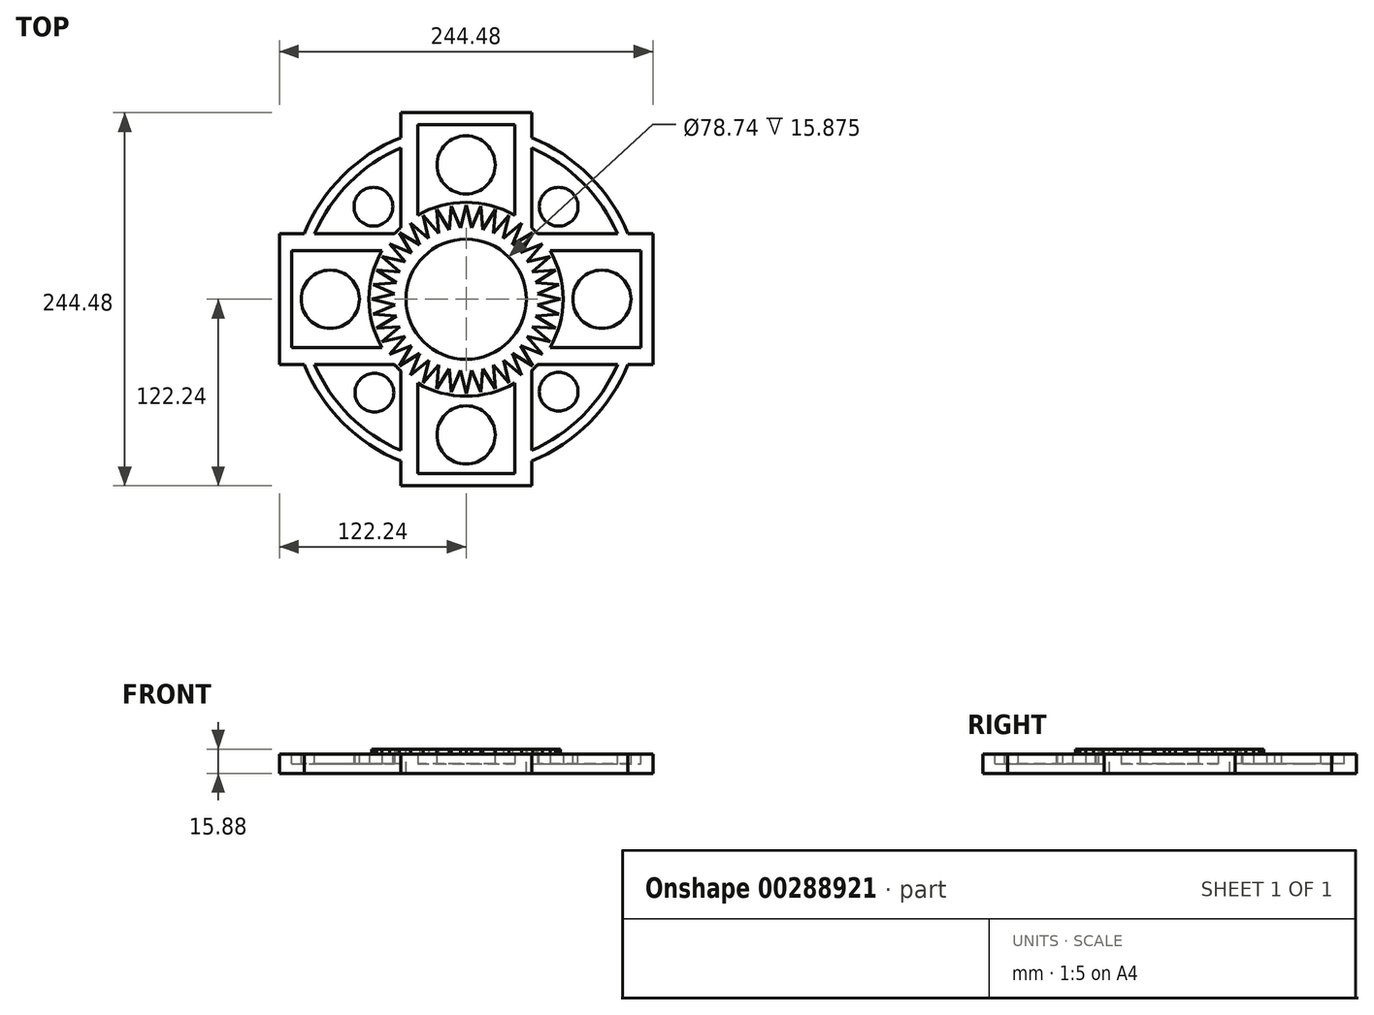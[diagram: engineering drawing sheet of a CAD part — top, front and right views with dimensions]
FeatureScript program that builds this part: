
annotation { "Feature Type Name" : "Feature", "Feature Type Description" : "" }
export const myFeature = defineFeature(function(context is Context, id is Id, definition is map)
    precondition{}
    {
        {
            var Q0;
            Q0=qCreatedBy(makeId("Top.planeOp"),FACE);
            var sketch = newSketch(context, id + "F0", { "sketchPlane" : qUnion([Q0])});
            skArc(sketch, "E0", {"start": v(-42.86, 105.96) * mm, "mid": v(-80.82, -80.82) * mm, "end": v(105.96, -42.86) * mm});
            skLineSegment(sketch, "E1.bottom", {"start": v(122.24, -122.24) * mm, "end": v(-122.24, -122.24) * mm, "construction": true});
            skLineSegment(sketch, "E1.top", {"start": v(122.24, 122.24) * mm, "end": v(-122.24, 122.24) * mm, "construction": true});
            skLineSegment(sketch, "E1.left", {"start": v(122.24, -122.24) * mm, "end": v(122.24, 122.24) * mm, "construction": true});
            skLineSegment(sketch, "E1.right", {"start": v(-122.24, -122.24) * mm, "end": v(-122.24, 122.24) * mm, "construction": true});
            skLineSegment(sketch, "E2.bottom", {"start": v(-42.86, 122.24) * mm, "end": v(42.86, 122.24) * mm});
            skLineSegment(sketch, "E2.top", {"start": v(-42.86, -122.24) * mm, "end": v(42.86, -122.24) * mm});
            skLineSegment(sketch, "E2.left", {"start": v(-42.86, 122.24) * mm, "end": v(-42.86, 105.96) * mm});
            skLineSegment(sketch, "E2.right", {"start": v(42.86, 122.24) * mm, "end": v(42.86, 105.96) * mm});
            skLineSegment(sketch, "E3.bottom", {"start": v(-122.24, 42.86) * mm, "end": v(-105.96, 42.86) * mm});
            skLineSegment(sketch, "E3.top", {"start": v(-122.24, -42.86) * mm, "end": v(-105.96, -42.86) * mm});
            skLineSegment(sketch, "E3.left", {"start": v(-122.24, 42.86) * mm, "end": v(-122.24, -42.86) * mm});
            skLineSegment(sketch, "E3.right", {"start": v(122.24, 42.86) * mm, "end": v(122.24, -42.86) * mm});
            skLineSegment(sketch, "E4.trimOffspring", {"start": v(105.96, 42.86) * mm, "end": v(122.24, 42.86) * mm});
            skArc(sketch, "E5.trimOffspring", {"start": v(105.96, 42.86) * mm, "mid": v(80.82, 80.82) * mm, "end": v(42.86, 105.96) * mm});
            skLineSegment(sketch, "E6.trimOffspring", {"start": v(105.96, -42.86) * mm, "end": v(122.24, -42.86) * mm});
            skLineSegment(sketch, "E7.trimOffspring", {"start": v(42.86, -105.96) * mm, "end": v(42.86, -122.24) * mm});
            skLineSegment(sketch, "E8.trimOffspring", {"start": v(-42.86, -105.96) * mm, "end": v(-42.86, -122.24) * mm});
            skSolve(sketch);
        }
        {
            var Q0;
            Q0 = qSketchRegion(id + "F0", true);
            extrude(context, id + "F1", {"entities" : qUnion([Q0]), "depth" : 12.7 * mm});
        }
        {
            var Q0;
            Q0=makeQuery(id+"F1.opExtrude","CAP_FACE",FACE,{"disambiguationData":[OSD([sQuery(id+"F0.wireOp",EDGE,"E0"),sQuery(id+"F0.wireOp",EDGE,"E2.bottom"),sQuery(id+"F0.wireOp",EDGE,"E2.top"),sQuery(id+"F0.wireOp",EDGE,"E2.left"),sQuery(id+"F0.wireOp",EDGE,"E2.right"),sQuery(id+"F0.wireOp",EDGE,"E3.bottom"),sQuery(id+"F0.wireOp",EDGE,"E3.top"),sQuery(id+"F0.wireOp",EDGE,"E3.left"),sQuery(id+"F0.wireOp",EDGE,"E3.right"),sQuery(id+"F0.wireOp",EDGE,"E4.trimOffspring"),sQuery(id+"F0.wireOp",EDGE,"E5.trimOffspring"),sQuery(id+"F0.wireOp",EDGE,"E6.trimOffspring"),sQuery(id+"F0.wireOp",EDGE,"E7.trimOffspring"),sQuery(id+"F0.wireOp",EDGE,"E8.trimOffspring")])],"isStart":false});
            var sketch = newSketch(context, id + "F2", { "sketchPlane" : qUnion([Q0])});
            skCircle(sketch, "E9", {"center": v(0, 0) * mm, "radius": 39.37 * mm});
            skSolve(sketch);
        }
        {
            var Q0;
            Q0 = qSketchRegion(id + "F2", true);
            extrude(context, id + "F3", {"entities" : qUnion([Q0]), "operationType" : NewBodyOperationType.REMOVE, "endBound" : BoundingType.UP_TO_NEXT, "oppositeDirection" : true, "depth" : 25.4 * mm});
        }
        {
            var Q0;
            Q0=makeQuery(id+"F1.opExtrude","CAP_FACE",FACE,{"disambiguationData":[OSD([sQuery(id+"F0.wireOp",EDGE,"E0"),sQuery(id+"F0.wireOp",EDGE,"E2.bottom"),sQuery(id+"F0.wireOp",EDGE,"E2.top"),sQuery(id+"F0.wireOp",EDGE,"E2.left"),sQuery(id+"F0.wireOp",EDGE,"E2.right"),sQuery(id+"F0.wireOp",EDGE,"E3.bottom"),sQuery(id+"F0.wireOp",EDGE,"E3.top"),sQuery(id+"F0.wireOp",EDGE,"E3.left"),sQuery(id+"F0.wireOp",EDGE,"E3.right"),sQuery(id+"F0.wireOp",EDGE,"E4.trimOffspring"),sQuery(id+"F0.wireOp",EDGE,"E5.trimOffspring"),sQuery(id+"F0.wireOp",EDGE,"E6.trimOffspring"),sQuery(id+"F0.wireOp",EDGE,"E7.trimOffspring"),sQuery(id+"F0.wireOp",EDGE,"E8.trimOffspring")])],"isStart":false});
            var sketch = newSketch(context, id + "F4", { "sketchPlane" : qUnion([Q0])});
            skLineSegment(sketch, "E10.bottom", {"start": v(-31.75, 114.3) * mm, "end": v(31.75, 114.3) * mm});
            skLineSegment(sketch, "E10.top", {"start": v(-31.75, -114.3) * mm, "end": v(31.75, -114.3) * mm});
            skLineSegment(sketch, "E10.left", {"start": v(-31.75, 114.3) * mm, "end": v(-31.75, 31.75) * mm});
            skLineSegment(sketch, "E10.right", {"start": v(31.75, 114.3) * mm, "end": v(31.75, 31.75) * mm});
            skPoint(sketch, "E10.middle", {"position": v(0, 0) * mm});
            skLineSegment(sketch, "E11.bottom", {"start": v(-114.3, -31.75) * mm, "end": v(-31.75, -31.75) * mm});
            skLineSegment(sketch, "E11.top", {"start": v(-114.3, 31.75) * mm, "end": v(-31.75, 31.75) * mm});
            skLineSegment(sketch, "E11.left", {"start": v(-114.3, -31.75) * mm, "end": v(-114.3, 31.75) * mm});
            skLineSegment(sketch, "E11.right", {"start": v(114.3, -31.75) * mm, "end": v(114.3, 31.75) * mm});
            skArc(sketch, "E12", {"start": v(-99.08, -42.86) * mm, "mid": v(-76.33, -76.33) * mm, "end": v(-42.86, -99.08) * mm});
            skArc(sketch, "E13.trimOffspring", {"start": v(99.08, 42.86) * mm, "mid": v(76.33, 76.33) * mm, "end": v(42.86, 99.08) * mm});
            skLineSegment(sketch, "E14.trimOffspring", {"start": v(31.75, -42.86) * mm, "end": v(31.75, -114.3) * mm});
            skLineSegment(sketch, "E15.trimOffspring", {"start": v(-31.75, -42.86) * mm, "end": v(-31.75, -114.3) * mm});
            skLineSegment(sketch, "E16.trimOffspring", {"start": v(31.75, 31.75) * mm, "end": v(114.3, 31.75) * mm});
            skArc(sketch, "E17.trimOffspring", {"start": v(-42.86, 99.08) * mm, "mid": v(-76.33, 76.33) * mm, "end": v(-99.08, 42.86) * mm});
            skLineSegment(sketch, "E18.trimOffspring", {"start": v(42.86, -31.75) * mm, "end": v(114.3, -31.75) * mm});
            skArc(sketch, "E19.trimOffspring", {"start": v(42.86, -99.08) * mm, "mid": v(76.33, -76.33) * mm, "end": v(99.08, -42.86) * mm});
            skLineSegment(sketch, "E20", {"start": v(105.96, 42.86) * mm, "end": v(42.86, 42.86) * mm});
            skLineSegment(sketch, "E21", {"start": v(-105.96, 42.86) * mm, "end": v(-42.86, 42.86) * mm});
            skLineSegment(sketch, "E22", {"start": v(-105.96, -42.86) * mm, "end": v(-42.86, -42.86) * mm});
            skLineSegment(sketch, "E23", {"start": v(-42.86, 105.96) * mm, "end": v(-42.86, 42.86) * mm});
            skLineSegment(sketch, "E24", {"start": v(42.86, 105.96) * mm, "end": v(42.86, 42.86) * mm});
            skLineSegment(sketch, "E25.trimOffspring", {"start": v(42.86, -42.86) * mm, "end": v(42.86, -105.96) * mm});
            skLineSegment(sketch, "E26.trimOffspring", {"start": v(-42.86, -42.86) * mm, "end": v(-42.86, -105.96) * mm});
            skLineSegment(sketch, "E27", {"start": v(-31.75, -42.86) * mm, "end": v(-31.75, -31.75) * mm});
            skLineSegment(sketch, "E28.trimOffspring", {"start": v(42.86, -42.86) * mm, "end": v(105.96, -42.86) * mm});
            skLineSegment(sketch, "E29", {"start": v(31.75, -42.86) * mm, "end": v(31.75, -31.75) * mm});
            skLineSegment(sketch, "E30", {"start": v(31.75, -31.75) * mm, "end": v(42.86, -31.75) * mm});
            skSolve(sketch);
        }
        {
            var Q0;
            Q0 = qSketchRegion(id + "F4", true);
            extrude(context, id + "F5", {"entities" : qUnion([Q0]), "operationType" : NewBodyOperationType.REMOVE, "oppositeDirection" : true, "depth" : 6.35 * mm});
        }
        {
            var Q0;
            Q0=makeQuery(id+"F5.boolean.opBoolean","COPY",FACE,{"derivedFrom":makeQuery(id+"F5.opExtrude","CAP_FACE",FACE,{"disambiguationData":[OSD([sQuery(id+"F4.wireOp",EDGE,"E10.bottom"),sQuery(id+"F4.wireOp",EDGE,"E10.top"),sQuery(id+"F4.wireOp",EDGE,"E10.left"),sQuery(id+"F4.wireOp",EDGE,"E10.right"),sQuery(id+"F4.wireOp",EDGE,"E11.bottom"),sQuery(id+"F4.wireOp",EDGE,"E11.top"),sQuery(id+"F4.wireOp",EDGE,"E11.left"),sQuery(id+"F4.wireOp",EDGE,"E11.right"),sQuery(id+"F4.wireOp",EDGE,"E14.trimOffspring"),sQuery(id+"F4.wireOp",EDGE,"E15.trimOffspring"),sQuery(id+"F4.wireOp",EDGE,"E16.trimOffspring"),sQuery(id+"F4.wireOp",EDGE,"E18.trimOffspring"),sQuery(id+"F4.wireOp",EDGE,"E27"),sQuery(id+"F4.wireOp",EDGE,"E29"),sQuery(id+"F4.wireOp",EDGE,"E30")])],"isStart":false})});
            var sketch = newSketch(context, id + "F6", { "sketchPlane" : qUnion([Q0])});
            skCircle(sketch, "E31", {"center": v(0, 0) * mm, "radius": 39.37 * mm});
            skCircle(sketch, "E32", {"center": v(0, 0) * mm, "radius": 63.5 * mm});
            skSolve(sketch);
        }
        {
            var Q0;
            Q0 = qSketchRegion(id + "F6", true);
            extrude(context, id + "F7", {"entities" : qUnion([Q0]), "operationType" : NewBodyOperationType.ADD, "depth" : 6.35 * mm});
        }
        {
            var Q0;
            Q0=makeQuery(id+"F7.boolean.opBoolean","MERGE",FACE,{"derivedFrom":[makeQuery(id+"F1.opExtrude","CAP_FACE",FACE,{"disambiguationData":[OSD([sQuery(id+"F0.wireOp",EDGE,"E0"),sQuery(id+"F0.wireOp",EDGE,"E2.bottom"),sQuery(id+"F0.wireOp",EDGE,"E2.top"),sQuery(id+"F0.wireOp",EDGE,"E2.left"),sQuery(id+"F0.wireOp",EDGE,"E2.right"),sQuery(id+"F0.wireOp",EDGE,"E3.bottom"),sQuery(id+"F0.wireOp",EDGE,"E3.top"),sQuery(id+"F0.wireOp",EDGE,"E3.left"),sQuery(id+"F0.wireOp",EDGE,"E3.right"),sQuery(id+"F0.wireOp",EDGE,"E4.trimOffspring"),sQuery(id+"F0.wireOp",EDGE,"E5.trimOffspring"),sQuery(id+"F0.wireOp",EDGE,"E6.trimOffspring"),sQuery(id+"F0.wireOp",EDGE,"E7.trimOffspring"),sQuery(id+"F0.wireOp",EDGE,"E8.trimOffspring")])],"isStart":false}),makeQuery(id+"F7.opExtrude","CAP_FACE",FACE,{"disambiguationData":[OSD([sQuery(id+"F6.wireOp",EDGE,"E31"),sQuery(id+"F6.wireOp",EDGE,"E32")])],"isStart":false})]});
            var sketch = newSketch(context, id + "F8", { "sketchPlane" : qUnion([Q0])});
            skLineSegment(sketch, "E33", {"start": v(0, 61.7) * mm, "end": v(-5.58, 38.97) * mm});
            skPoint(sketch, "E33.startSnap0", {"position": v(0, 63.5) * mm});
            skLineSegment(sketch, "E34", {"start": v(0, 61.7) * mm, "end": v(5.53, 38.98) * mm});
            skLineSegment(sketch, "E35.1.0", {"start": v(-9.65, 60.94) * mm, "end": v(-11.6, 37.62) * mm});
            skLineSegment(sketch, "E35.1.1", {"start": v(-9.65, 60.94) * mm, "end": v(-0.64, 39.36) * mm});
            skLineSegment(sketch, "E35.2.0", {"start": v(-19.06, 58.68) * mm, "end": v(-17.35, 35.34) * mm});
            skLineSegment(sketch, "E35.2.1", {"start": v(-19.06, 58.68) * mm, "end": v(-6.79, 38.78) * mm});
            skLineSegment(sketch, "E35.3.0", {"start": v(-28, 54.97) * mm, "end": v(-22.66, 32.2) * mm});
            skLineSegment(sketch, "E35.3.1", {"start": v(-28, 54.97) * mm, "end": v(-12.77, 37.24) * mm});
            skLineSegment(sketch, "E35.4.0", {"start": v(-36.26, 49.91) * mm, "end": v(-27.42, 28.25) * mm});
            skLineSegment(sketch, "E35.4.1", {"start": v(-36.26, 49.91) * mm, "end": v(-18.44, 34.78) * mm});
            skLineSegment(sketch, "E35.5.0", {"start": v(-43.63, 43.63) * mm, "end": v(-31.5, 23.61) * mm});
            skLineSegment(sketch, "E35.5.1", {"start": v(-43.63, 43.63) * mm, "end": v(-23.66, 31.47) * mm});
            skLineSegment(sketch, "E35.6.0", {"start": v(-49.91, 36.26) * mm, "end": v(-34.8, 18.4) * mm});
            skLineSegment(sketch, "E35.6.1", {"start": v(-49.91, 36.26) * mm, "end": v(-28.29, 27.38) * mm});
            skLineSegment(sketch, "E35.7.0", {"start": v(-54.97, 28) * mm, "end": v(-37.26, 12.72) * mm});
            skLineSegment(sketch, "E35.7.1", {"start": v(-54.97, 28) * mm, "end": v(-32.22, 22.62) * mm});
            skLineSegment(sketch, "E35.8.0", {"start": v(-58.68, 19.06) * mm, "end": v(-38.79, 6.74) * mm});
            skLineSegment(sketch, "E35.8.1", {"start": v(-58.68, 19.06) * mm, "end": v(-35.36, 17.3) * mm});
            skLineSegment(sketch, "E35.9.0", {"start": v(-60.94, 9.65) * mm, "end": v(-39.37, 0.59) * mm});
            skLineSegment(sketch, "E35.9.1", {"start": v(-60.94, 9.65) * mm, "end": v(-37.64, 11.56) * mm});
            skLineSegment(sketch, "E35.10.0", {"start": v(-61.7, 0) * mm, "end": v(-38.97, -5.58) * mm});
            skLineSegment(sketch, "E35.10.1", {"start": v(-61.7, 0) * mm, "end": v(-38.98, 5.53) * mm});
            skLineSegment(sketch, "E35.11.0", {"start": v(-60.94, -9.65) * mm, "end": v(-37.62, -11.6) * mm});
            skLineSegment(sketch, "E35.11.1", {"start": v(-60.94, -9.65) * mm, "end": v(-39.36, -0.64) * mm});
            skLineSegment(sketch, "E35.12.0", {"start": v(-58.68, -19.06) * mm, "end": v(-35.34, -17.35) * mm});
            skLineSegment(sketch, "E35.12.1", {"start": v(-58.68, -19.06) * mm, "end": v(-38.78, -6.79) * mm});
            skLineSegment(sketch, "E35.13.0", {"start": v(-54.97, -28) * mm, "end": v(-32.2, -22.66) * mm});
            skLineSegment(sketch, "E35.13.1", {"start": v(-54.97, -28) * mm, "end": v(-37.24, -12.77) * mm});
            skLineSegment(sketch, "E35.14.0", {"start": v(-49.91, -36.26) * mm, "end": v(-28.25, -27.42) * mm});
            skLineSegment(sketch, "E35.14.1", {"start": v(-49.91, -36.26) * mm, "end": v(-34.78, -18.44) * mm});
            skLineSegment(sketch, "E35.15.0", {"start": v(-43.63, -43.63) * mm, "end": v(-23.61, -31.5) * mm});
            skLineSegment(sketch, "E35.15.1", {"start": v(-43.63, -43.63) * mm, "end": v(-31.47, -23.66) * mm});
            skLineSegment(sketch, "E35.16.0", {"start": v(-36.26, -49.91) * mm, "end": v(-18.4, -34.8) * mm});
            skLineSegment(sketch, "E35.16.1", {"start": v(-36.26, -49.91) * mm, "end": v(-27.38, -28.29) * mm});
            skLineSegment(sketch, "E35.17.0", {"start": v(-28, -54.97) * mm, "end": v(-12.72, -37.26) * mm});
            skLineSegment(sketch, "E35.17.1", {"start": v(-28, -54.97) * mm, "end": v(-22.62, -32.22) * mm});
            skLineSegment(sketch, "E35.18.0", {"start": v(-19.06, -58.68) * mm, "end": v(-6.74, -38.79) * mm});
            skLineSegment(sketch, "E35.18.1", {"start": v(-19.06, -58.68) * mm, "end": v(-17.3, -35.36) * mm});
            skLineSegment(sketch, "E35.19.0", {"start": v(-9.65, -60.94) * mm, "end": v(-0.59, -39.37) * mm});
            skLineSegment(sketch, "E35.19.1", {"start": v(-9.65, -60.94) * mm, "end": v(-11.56, -37.64) * mm});
            skLineSegment(sketch, "E35.20.0", {"start": v(0, -61.7) * mm, "end": v(5.58, -38.97) * mm});
            skLineSegment(sketch, "E35.20.1", {"start": v(0, -61.7) * mm, "end": v(-5.53, -38.98) * mm});
            skLineSegment(sketch, "E35.21.0", {"start": v(9.65, -60.94) * mm, "end": v(11.6, -37.62) * mm});
            skLineSegment(sketch, "E35.21.1", {"start": v(9.65, -60.94) * mm, "end": v(0.64, -39.36) * mm});
            skLineSegment(sketch, "E35.22.0", {"start": v(19.06, -58.68) * mm, "end": v(17.35, -35.34) * mm});
            skLineSegment(sketch, "E35.22.1", {"start": v(19.06, -58.68) * mm, "end": v(6.79, -38.78) * mm});
            skLineSegment(sketch, "E35.23.0", {"start": v(28, -54.97) * mm, "end": v(22.66, -32.2) * mm});
            skLineSegment(sketch, "E35.23.1", {"start": v(28, -54.97) * mm, "end": v(12.77, -37.24) * mm});
            skLineSegment(sketch, "E35.24.0", {"start": v(36.26, -49.91) * mm, "end": v(27.42, -28.25) * mm});
            skLineSegment(sketch, "E35.24.1", {"start": v(36.26, -49.91) * mm, "end": v(18.44, -34.78) * mm});
            skLineSegment(sketch, "E35.25.0", {"start": v(43.63, -43.63) * mm, "end": v(31.5, -23.61) * mm});
            skLineSegment(sketch, "E35.25.1", {"start": v(43.63, -43.63) * mm, "end": v(23.66, -31.47) * mm});
            skLineSegment(sketch, "E35.26.0", {"start": v(49.91, -36.26) * mm, "end": v(34.8, -18.4) * mm});
            skLineSegment(sketch, "E35.26.1", {"start": v(49.91, -36.26) * mm, "end": v(28.29, -27.38) * mm});
            skLineSegment(sketch, "E35.27.0", {"start": v(54.97, -28) * mm, "end": v(37.26, -12.72) * mm});
            skLineSegment(sketch, "E35.27.1", {"start": v(54.97, -28) * mm, "end": v(32.22, -22.62) * mm});
            skLineSegment(sketch, "E35.28.0", {"start": v(58.68, -19.06) * mm, "end": v(38.79, -6.74) * mm});
            skLineSegment(sketch, "E35.28.1", {"start": v(58.68, -19.06) * mm, "end": v(35.36, -17.3) * mm});
            skLineSegment(sketch, "E35.29.0", {"start": v(60.94, -9.65) * mm, "end": v(39.37, -0.59) * mm});
            skLineSegment(sketch, "E35.29.1", {"start": v(60.94, -9.65) * mm, "end": v(37.64, -11.56) * mm});
            skLineSegment(sketch, "E35.30.0", {"start": v(61.7, 0) * mm, "end": v(38.97, 5.58) * mm});
            skLineSegment(sketch, "E35.30.1", {"start": v(61.7, 0) * mm, "end": v(38.98, -5.53) * mm});
            skLineSegment(sketch, "E35.31.0", {"start": v(60.94, 9.65) * mm, "end": v(37.62, 11.6) * mm});
            skLineSegment(sketch, "E35.31.1", {"start": v(60.94, 9.65) * mm, "end": v(39.36, 0.64) * mm});
            skLineSegment(sketch, "E35.32.0", {"start": v(58.68, 19.06) * mm, "end": v(35.34, 17.35) * mm});
            skLineSegment(sketch, "E35.32.1", {"start": v(58.68, 19.06) * mm, "end": v(38.78, 6.79) * mm});
            skLineSegment(sketch, "E35.33.0", {"start": v(54.97, 28) * mm, "end": v(32.2, 22.66) * mm});
            skLineSegment(sketch, "E35.33.1", {"start": v(54.97, 28) * mm, "end": v(37.24, 12.77) * mm});
            skLineSegment(sketch, "E35.34.0", {"start": v(49.91, 36.26) * mm, "end": v(28.25, 27.42) * mm});
            skLineSegment(sketch, "E35.34.1", {"start": v(49.91, 36.26) * mm, "end": v(34.78, 18.44) * mm});
            skLineSegment(sketch, "E35.35.0", {"start": v(43.63, 43.63) * mm, "end": v(23.61, 31.5) * mm});
            skLineSegment(sketch, "E35.35.1", {"start": v(43.63, 43.63) * mm, "end": v(31.47, 23.66) * mm});
            skLineSegment(sketch, "E35.36.0", {"start": v(36.26, 49.91) * mm, "end": v(18.4, 34.8) * mm});
            skLineSegment(sketch, "E35.36.1", {"start": v(36.26, 49.91) * mm, "end": v(27.38, 28.29) * mm});
            skLineSegment(sketch, "E35.37.0", {"start": v(28, 54.97) * mm, "end": v(12.72, 37.26) * mm});
            skLineSegment(sketch, "E35.37.1", {"start": v(28, 54.97) * mm, "end": v(22.62, 32.22) * mm});
            skLineSegment(sketch, "E35.38.0", {"start": v(19.06, 58.68) * mm, "end": v(6.74, 38.79) * mm});
            skLineSegment(sketch, "E35.38.1", {"start": v(19.06, 58.68) * mm, "end": v(17.3, 35.36) * mm});
            skLineSegment(sketch, "E35.39.0", {"start": v(9.65, 60.94) * mm, "end": v(0.59, 39.37) * mm});
            skLineSegment(sketch, "E35.39.1", {"start": v(9.65, 60.94) * mm, "end": v(11.56, 37.64) * mm});
            skPoint(sketch, "E35.center", {"position": v(0, 0) * mm});
            skSolve(sketch);
        }
        {
            var Q0;
            Q0 = qSketchRegion(id + "F8", true);
            extrude(context, id + "F9", {"entities" : qUnion([Q0]), "operationType" : NewBodyOperationType.ADD, "depth" : 3.17 * mm});
        }
        {
            var Q0;
            Q0=makeQuery(id+"F9.opExtrude","CAP_FACE",FACE,{"disambiguationData":[OSD([sQuery(id+"F8.wireOp",EDGE,"E33"),sQuery(id+"F8.wireOp",EDGE,"E34"),sQuery(id+"F8.wireOp",EDGE,"E35.1.0"),sQuery(id+"F8.wireOp",EDGE,"E35.1.1"),sQuery(id+"F8.wireOp",EDGE,"E35.2.0"),sQuery(id+"F8.wireOp",EDGE,"E35.2.1"),sQuery(id+"F8.wireOp",EDGE,"E35.3.0"),sQuery(id+"F8.wireOp",EDGE,"E35.3.1"),sQuery(id+"F8.wireOp",EDGE,"E35.4.0"),sQuery(id+"F8.wireOp",EDGE,"E35.4.1"),sQuery(id+"F8.wireOp",EDGE,"E35.5.0"),sQuery(id+"F8.wireOp",EDGE,"E35.5.1"),sQuery(id+"F8.wireOp",EDGE,"E35.6.0"),sQuery(id+"F8.wireOp",EDGE,"E35.6.1"),sQuery(id+"F8.wireOp",EDGE,"E35.7.0"),sQuery(id+"F8.wireOp",EDGE,"E35.7.1"),sQuery(id+"F8.wireOp",EDGE,"E35.8.0"),sQuery(id+"F8.wireOp",EDGE,"E35.8.1"),sQuery(id+"F8.wireOp",EDGE,"E35.9.0"),sQuery(id+"F8.wireOp",EDGE,"E35.9.1"),sQuery(id+"F8.wireOp",EDGE,"E35.10.0"),sQuery(id+"F8.wireOp",EDGE,"E35.10.1"),sQuery(id+"F8.wireOp",EDGE,"E35.11.0"),sQuery(id+"F8.wireOp",EDGE,"E35.11.1"),sQuery(id+"F8.wireOp",EDGE,"E35.12.0"),sQuery(id+"F8.wireOp",EDGE,"E35.12.1"),sQuery(id+"F8.wireOp",EDGE,"E35.13.0"),sQuery(id+"F8.wireOp",EDGE,"E35.13.1"),sQuery(id+"F8.wireOp",EDGE,"E35.14.0"),sQuery(id+"F8.wireOp",EDGE,"E35.14.1"),sQuery(id+"F8.wireOp",EDGE,"E35.15.0"),sQuery(id+"F8.wireOp",EDGE,"E35.15.1"),sQuery(id+"F8.wireOp",EDGE,"E35.16.0"),sQuery(id+"F8.wireOp",EDGE,"E35.16.1"),sQuery(id+"F8.wireOp",EDGE,"E35.17.0"),sQuery(id+"F8.wireOp",EDGE,"E35.17.1"),sQuery(id+"F8.wireOp",EDGE,"E35.18.0"),sQuery(id+"F8.wireOp",EDGE,"E35.18.1"),sQuery(id+"F8.wireOp",EDGE,"E35.19.0"),sQuery(id+"F8.wireOp",EDGE,"E35.19.1"),sQuery(id+"F8.wireOp",EDGE,"E35.20.0"),sQuery(id+"F8.wireOp",EDGE,"E35.20.1"),sQuery(id+"F8.wireOp",EDGE,"E35.21.0"),sQuery(id+"F8.wireOp",EDGE,"E35.21.1"),sQuery(id+"F8.wireOp",EDGE,"E35.22.0"),sQuery(id+"F8.wireOp",EDGE,"E35.22.1"),sQuery(id+"F8.wireOp",EDGE,"E35.23.0"),sQuery(id+"F8.wireOp",EDGE,"E35.23.1"),sQuery(id+"F8.wireOp",EDGE,"E35.24.0"),sQuery(id+"F8.wireOp",EDGE,"E35.24.1"),sQuery(id+"F8.wireOp",EDGE,"E35.25.0"),sQuery(id+"F8.wireOp",EDGE,"E35.25.1"),sQuery(id+"F8.wireOp",EDGE,"E35.26.0"),sQuery(id+"F8.wireOp",EDGE,"E35.26.1"),sQuery(id+"F8.wireOp",EDGE,"E35.27.0"),sQuery(id+"F8.wireOp",EDGE,"E35.27.1"),sQuery(id+"F8.wireOp",EDGE,"E35.28.0"),sQuery(id+"F8.wireOp",EDGE,"E35.28.1"),sQuery(id+"F8.wireOp",EDGE,"E35.29.0"),sQuery(id+"F8.wireOp",EDGE,"E35.29.1"),sQuery(id+"F8.wireOp",EDGE,"E35.30.0"),sQuery(id+"F8.wireOp",EDGE,"E35.30.1"),sQuery(id+"F8.wireOp",EDGE,"E35.31.0"),sQuery(id+"F8.wireOp",EDGE,"E35.31.1"),sQuery(id+"F8.wireOp",EDGE,"E35.32.0"),sQuery(id+"F8.wireOp",EDGE,"E35.32.1"),sQuery(id+"F8.wireOp",EDGE,"E35.33.0"),sQuery(id+"F8.wireOp",EDGE,"E35.33.1"),sQuery(id+"F8.wireOp",EDGE,"E35.34.0"),sQuery(id+"F8.wireOp",EDGE,"E35.34.1"),sQuery(id+"F8.wireOp",EDGE,"E35.35.0"),sQuery(id+"F8.wireOp",EDGE,"E35.35.1"),sQuery(id+"F8.wireOp",EDGE,"E35.36.0"),sQuery(id+"F8.wireOp",EDGE,"E35.36.1"),sQuery(id+"F8.wireOp",EDGE,"E35.37.0"),sQuery(id+"F8.wireOp",EDGE,"E35.37.1"),sQuery(id+"F8.wireOp",EDGE,"E35.38.0"),sQuery(id+"F8.wireOp",EDGE,"E35.38.1"),sQuery(id+"F8.wireOp",EDGE,"E35.39.0"),sQuery(id+"F8.wireOp",EDGE,"E35.39.1")])],"isStart":false});
            var sketch = newSketch(context, id + "F10", { "sketchPlane" : qUnion([Q0])});
            skCircle(sketch, "E36", {"center": v(0, 0) * mm, "radius": 39.37 * mm});
            skSolve(sketch);
        }
        {
            var Q0;
            Q0 = qSketchRegion(id + "F10", true);
            extrude(context, id + "F11", {"entities" : qUnion([Q0]), "operationType" : NewBodyOperationType.REMOVE, "endBound" : BoundingType.UP_TO_NEXT, "oppositeDirection" : true, "depth" : 25.4 * mm});
        }
        {
            var Q0;
            Q0=makeQuery(id+"F7.boolean.opBoolean","MERGE",FACE,{"derivedFrom":[makeQuery(id+"F1.opExtrude","CAP_FACE",FACE,{"disambiguationData":[OSD([sQuery(id+"F0.wireOp",EDGE,"E0"),sQuery(id+"F0.wireOp",EDGE,"E2.bottom"),sQuery(id+"F0.wireOp",EDGE,"E2.top"),sQuery(id+"F0.wireOp",EDGE,"E2.left"),sQuery(id+"F0.wireOp",EDGE,"E2.right"),sQuery(id+"F0.wireOp",EDGE,"E3.bottom"),sQuery(id+"F0.wireOp",EDGE,"E3.top"),sQuery(id+"F0.wireOp",EDGE,"E3.left"),sQuery(id+"F0.wireOp",EDGE,"E3.right"),sQuery(id+"F0.wireOp",EDGE,"E4.trimOffspring"),sQuery(id+"F0.wireOp",EDGE,"E5.trimOffspring"),sQuery(id+"F0.wireOp",EDGE,"E6.trimOffspring"),sQuery(id+"F0.wireOp",EDGE,"E7.trimOffspring"),sQuery(id+"F0.wireOp",EDGE,"E8.trimOffspring")])],"isStart":false}),makeQuery(id+"F7.opExtrude","CAP_FACE",FACE,{"disambiguationData":[OSD([sQuery(id+"F6.wireOp",EDGE,"E31"),sQuery(id+"F6.wireOp",EDGE,"E32")])],"isStart":false})]});
            var sketch = newSketch(context, id + "F12", { "sketchPlane" : qUnion([Q0])});
            skLineSegment(sketch, "E37", {"start": v(0, 114.3) * mm, "end": v(0, 61.7) * mm, "construction": true});
            skLineSegment(sketch, "E38", {"start": v(0, 61.7) * mm, "end": v(44.9, 44.9) * mm, "construction": true});
            skLineSegment(sketch, "E39", {"start": v(44.9, 44.9) * mm, "end": v(76.33, 76.33) * mm, "construction": true});
            skLineSegment(sketch, "E40", {"start": v(76.33, 76.33) * mm, "end": v(114.3, 0) * mm, "construction": true});
            skLineSegment(sketch, "E41", {"start": v(114.3, 0) * mm, "end": v(63.5, 0) * mm, "construction": true});
            skLineSegment(sketch, "E42", {"start": v(63.5, 0) * mm, "end": v(44.9, -44.9) * mm, "construction": true});
            skLineSegment(sketch, "E43", {"start": v(44.9, -44.9) * mm, "end": v(76.33, -76.33) * mm, "construction": true});
            skLineSegment(sketch, "E44", {"start": v(76.33, -76.33) * mm, "end": v(0, -114.3) * mm, "construction": true});
            skLineSegment(sketch, "E45", {"start": v(0, -114.3) * mm, "end": v(0, -63.5) * mm, "construction": true});
            skLineSegment(sketch, "E46", {"start": v(0, -63.5) * mm, "end": v(-43.63, -46.14) * mm, "construction": true});
            skLineSegment(sketch, "E47", {"start": v(-43.63, -46.14) * mm, "end": v(-76.33, -76.33) * mm, "construction": true});
            skLineSegment(sketch, "E48", {"start": v(-76.33, -76.33) * mm, "end": v(-114.3, 0) * mm, "construction": true});
            skLineSegment(sketch, "E49", {"start": v(-114.3, 0) * mm, "end": v(-63.5, 0) * mm, "construction": true});
            skLineSegment(sketch, "E50", {"start": v(-63.5, 0) * mm, "end": v(-44.9, 44.9) * mm, "construction": true});
            skLineSegment(sketch, "E51", {"start": v(-44.9, 44.9) * mm, "end": v(-76.33, 76.33) * mm, "construction": true});
            skCircle(sketch, "E52", {"center": v(0, 88) * mm, "radius": 19.05 * mm});
            skCircle(sketch, "E53", {"center": v(60.62, 60.62) * mm, "radius": 12.7 * mm});
            skCircle(sketch, "E54", {"center": v(88.9, 0) * mm, "radius": 19.05 * mm});
            skCircle(sketch, "E55", {"center": v(60.62, -60.62) * mm, "radius": 12.7 * mm});
            skCircle(sketch, "E56", {"center": v(0, -88.9) * mm, "radius": 19.05 * mm});
            skCircle(sketch, "E57", {"center": v(-59.98, -61.24) * mm, "radius": 12.7 * mm});
            skCircle(sketch, "E58", {"center": v(-88.9, 0) * mm, "radius": 19.05 * mm});
            skCircle(sketch, "E59", {"center": v(-60.62, 60.62) * mm, "radius": 12.7 * mm});
            skSolve(sketch);
        }
        {
            var Q0;
            Q0 = qSketchRegion(id + "F12", true);
            extrude(context, id + "F13", {"entities" : qUnion([Q0]), "operationType" : NewBodyOperationType.ADD, "oppositeDirection" : true, "depth" : 6.35 * mm});
        }
    });
